# Revit family: 879-102X99-001-DN50-200
name_source: partatom
category: Pipe Accessories
units: mm (PartAtom-declared; Revit-internal decimal feet)

## family parameters
Always vertical = Yes
Cut with Voids When Loaded = No
Part Type = Valve - Breaks Into
Round Connector Dimension = Use Diameter
Shared = No
Work Plane-Based = No

## types (48) — shared parameters
879-0050-10-14400209999 = DN50_PN10/16
879-0050-10-144002099A0 = DN50_PN10/16
879-0050-10-14400219999 = DN50_PN10/16
879-0050-10-144002199A0 = DN50_PN10/16
879-0050-10-14400229999 = DN50_PN10/16
879-0050-10-144002299A0 = DN50_PN10/16
879-0065-10-14400209999 = DN65_PN10/16
879-0065-10-144002099A0 = DN65_PN10/16
879-0065-10-14400219999 = DN65_PN10/16
879-0065-10-144002199A0 = DN65_PN10/16
879-0065-10-14400229999 = DN65_PN10/16
879-0065-10-144002299A0 = DN65_PN10/16
879-0080-10-14400209999 = DN80_PN10/16
879-0080-10-144002099A0 = DN80_PN10/16
879-0080-10-14400219999 = DN80_PN10/16
879-0080-10-144002199A0 = DN80_PN10/16
879-0080-10-14400229999 = DN80_PN10/16
879-0080-10-144002299A0 = DN80_PN10/16
879-0100-10-14400209999 = DN100_PN10/16
879-0100-10-144002099A0 = DN100_PN10/16
879-0100-10-14400219999 = DN100_PN10/16
879-0100-10-144002199A0 = DN100_PN10/16
879-0100-10-14400229999 = DN100_PN10/16
879-0100-10-144002299A0 = DN100_PN10/16
879-0150-10-14400209999 = DN150_PN10/16
879-0150-10-144002099A0 = DN150_PN10/16
879-0150-10-14400219999 = DN150_PN10/16
879-0150-10-144002199A0 = DN150_PN10/16
879-0150-10-14400229999 = DN150_PN10/16
879-0150-10-144002299A0 = DN150_PN10/16
879-0150-10-14400239999 = DN150_PN10/16
879-0150-10-144002399A0 = DN150_PN10/16
879-0200-10-04400209999 = DN200_PN10
879-0200-10-044002099A0 = DN200_PN10
879-0200-10-04400219999 = DN200_PN10
879-0200-10-044002199A0 = DN200_PN10
879-0200-10-04400229999 = DN200_PN10
879-0200-10-044002299A0 = DN200_PN10
879-0200-10-04400239999 = DN200_PN10
879-0200-10-044002399A0 = DN200_PN10
879-0200-10-14400209999 = DN200_PN16
879-0200-10-144002099A0 = DN200_PN16
879-0200-10-14400219999 = DN200_PN16
879-0200-10-144002199A0 = DN200_PN16
879-0200-10-14400229999 = DN200_PN16
879-0200-10-144002299A0 = DN200_PN16
879-0200-10-14400239999 = DN200_PN16
879-0200-10-144002399A0 = DN200_PN16
Body_wall_thickness = 10 mm  [stored 0.0328084 ft]
Description_ = AVK CONSTANT FLOW CONTROL VALVE
Search_Table = 879-102X99-001-DN50-200
URL product pages = https://www.avkvalves.com

## per-type parameters (varying)
- 879-0050-10-14400209999_DN50_PN10/16: Body_Collar_Dia=23.96 mm; Body_Collar_Dia_2=20.63 mm; Body_Flange_Dia=74.19 mm; Body_Flange_Dia_2=82.14 mm; Body_Height_1=57.5 mm; Body_Height_2=28.75 mm; Body_Height_3=45 mm; Body_Height_4=43.75 mm; Body_Top_Dia=10.31 mm; Body_Top_Dia_2=8.59 mm; Body_With_Dia=57.5 mm; Body_With_Dia_2=62.16 mm; Bolt_support=153.33 mm; Bolt_support_2=76.67 mm; Bolt_support_Dia=12 mm  [stored 0.0393701 ft]; Bolt_support_lenght=45 mm; Bolt_support_lenght_2=55 mm; Bottom_profile=12.5 mm  [stored 0.0410105 ft]; D1=49.5 mm; DN=50 mm; FOD=82.5 mm; Fillet_Length=6 mm  [stored 0.019685 ft]; Flange_thickness=19 mm; H3=400 mm; ID=25 mm; L=230 mm; L1=247 mm; L_Ref=238.5 mm; PG_Dia=25 mm; PG_Ref=38.33 mm; PG_depth=8.4 mm  [stored 0.0275591 ft]; PG_ref=35 mm; Pilot_Dia_1=15 mm  [stored 0.0492126 ft]; Pilot_Dia_2=30 mm; Pilot_Dia_3=10 mm  [stored 0.0328084 ft]; Pilot_Dia_4=5 mm  [stored 0.0164042 ft]; Pilot_Dia_5=3.33 mm; Pilot_top_1=241.88 mm; Pilot_top_ref=75.63 mm; Profile1_Height=135 mm; Profile1_Length=22.3 mm; Profile1_Length_2=14.86 mm; Profile_Dia=6 mm  [stored 0.019685 ft]; Profile_Dia_2=6 mm  [stored 0.019685 ft]; Profile_Dia_3=12 mm  [stored 0.0393701 ft]; Top_Profile=92 mm; Top_Profile_Ref=97 mm; Top_Ref=166.25 mm; Top_Ref_2=204.06 mm; W=245 mm; W_Ref=242 mm
- 879-0050-10-144002099A0_DN50_PN10/16: Body_Collar_Dia=23.96 mm; Body_Collar_Dia_2=20.63 mm; Body_Flange_Dia=74.19 mm; Body_Flange_Dia_2=82.14 mm; Body_Height_1=57.5 mm; Body_Height_2=28.75 mm; Body_Height_3=50 mm; Body_Height_4=43.75 mm; Body_Top_Dia=10.31 mm; Body_Top_Dia_2=8.59 mm; Body_With_Dia=57.5 mm; Body_With_Dia_2=62.16 mm; Bolt_support=153.33 mm; Bolt_support_2=76.67 mm; Bolt_support_Dia=12 mm  [stored 0.0393701 ft]; Bolt_support_lenght=45.05 mm; Bolt_support_lenght_2=55.05 mm; Bottom_profile=12.53 mm; D1=49.5 mm; DN=50.1 mm; FOD=82.5 mm; Fillet_Length=6 mm  [stored 0.019685 ft]; Flange_thickness=19 mm; H3=407 mm; ID=25.05 mm; L=230 mm; L1=247 mm; L_Ref=238.5 mm; PG_Dia=25.05 mm; PG_Ref=38.33 mm; PG_depth=8.4 mm  [stored 0.0275591 ft]; PG_ref=35.05 mm; Pilot_Dia_1=15 mm  [stored 0.0492126 ft]; Pilot_Dia_2=30 mm; Pilot_Dia_3=10 mm  [stored 0.0328084 ft]; Pilot_Dia_4=5 mm  [stored 0.0164042 ft]; Pilot_Dia_5=3.33 mm; Pilot_top_1=247.88 mm; Pilot_top_ref=76.63 mm; Profile1_Height=145 mm; Profile1_Length=22.3 mm; Profile1_Length_2=14.86 mm; Profile_Dia=6 mm  [stored 0.019685 ft]; Profile_Dia_2=6 mm  [stored 0.019685 ft]; Profile_Dia_3=12 mm  [stored 0.0393701 ft]; Top_Profile=92 mm; Top_Profile_Ref=97 mm; Top_Ref=171.25 mm; Top_Ref_2=209.56 mm; W=245 mm; W_Ref=242 mm
- 879-0050-10-14400219999_DN50_PN10/16: Body_Collar_Dia=23.96 mm; Body_Collar_Dia_2=20.63 mm; Body_Flange_Dia=74.19 mm; Body_Flange_Dia_2=82.14 mm; Body_Height_1=57.5 mm; Body_Height_2=28.75 mm; Body_Height_3=45 mm; Body_Height_4=43.75 mm; Body_Top_Dia=10.31 mm; Body_Top_Dia_2=8.59 mm; Body_With_Dia=57.5 mm; Body_With_Dia_2=62.16 mm; Bolt_support=153.33 mm; Bolt_support_2=76.67 mm; Bolt_support_Dia=12 mm  [stored 0.0393701 ft]; Bolt_support_lenght=45.1 mm; Bolt_support_lenght_2=55.1 mm; Bottom_profile=12.55 mm  [stored 0.0411745 ft]; D1=49.5 mm; DN=50.2 mm; FOD=82.5 mm; Fillet_Length=6 mm  [stored 0.019685 ft]; Flange_thickness=19 mm; H3=400 mm; ID=25.1 mm; L=230 mm; L1=247 mm; L_Ref=238.5 mm; PG_Dia=25.1 mm; PG_Ref=38.33 mm; PG_depth=8.4 mm  [stored 0.0275591 ft]; PG_ref=35.1 mm; Pilot_Dia_1=15 mm  [stored 0.0492126 ft]; Pilot_Dia_2=30 mm; Pilot_Dia_3=10 mm  [stored 0.0328084 ft]; Pilot_Dia_4=5 mm  [stored 0.0164042 ft]; Pilot_Dia_5=3.33 mm; Pilot_top_1=241.88 mm; Pilot_top_ref=75.63 mm; Profile1_Height=135 mm; Profile1_Length=22.3 mm; Profile1_Length_2=14.86 mm; Profile_Dia=6 mm  [stored 0.019685 ft]; Profile_Dia_2=6 mm  [stored 0.019685 ft]; Profile_Dia_3=12 mm  [stored 0.0393701 ft]; Top_Profile=92 mm; Top_Profile_Ref=97 mm; Top_Ref=166.25 mm; Top_Ref_2=204.06 mm; W=245 mm; W_Ref=242 mm
- 879-0050-10-144002199A0_DN50_PN10/16: Body_Collar_Dia=23.96 mm; Body_Collar_Dia_2=20.63 mm; Body_Flange_Dia=74.19 mm; Body_Flange_Dia_2=82.14 mm; Body_Height_1=57.5 mm; Body_Height_2=28.75 mm; Body_Height_3=50 mm; Body_Height_4=43.75 mm; Body_Top_Dia=10.31 mm; Body_Top_Dia_2=8.59 mm; Body_With_Dia=57.5 mm; Body_With_Dia_2=62.16 mm; Bolt_support=153.33 mm; Bolt_support_2=76.67 mm; Bolt_support_Dia=12 mm  [stored 0.0393701 ft]; Bolt_support_lenght=45.15 mm; Bolt_support_lenght_2=55.15 mm; Bottom_profile=12.58 mm; D1=49.5 mm; DN=50.3 mm; FOD=82.5 mm; Fillet_Length=6 mm  [stored 0.019685 ft]; Flange_thickness=19 mm; H3=407 mm; ID=25.15 mm; L=230 mm; L1=247 mm; L_Ref=238.5 mm; PG_Dia=25.15 mm; PG_Ref=38.33 mm; PG_depth=8.4 mm  [stored 0.0275591 ft]; PG_ref=35.15 mm; Pilot_Dia_1=15 mm  [stored 0.0492126 ft]; Pilot_Dia_2=30 mm; Pilot_Dia_3=10 mm  [stored 0.0328084 ft]; Pilot_Dia_4=5 mm  [stored 0.0164042 ft]; Pilot_Dia_5=3.33 mm; Pilot_top_1=247.88 mm; Pilot_top_ref=76.63 mm; Profile1_Height=145 mm; Profile1_Length=22.3 mm; Profile1_Length_2=14.86 mm; Profile_Dia=6 mm  [stored 0.019685 ft]; Profile_Dia_2=6 mm  [stored 0.019685 ft]; Profile_Dia_3=12 mm  [stored 0.0393701 ft]; Top_Profile=92 mm; Top_Profile_Ref=97 mm; Top_Ref=171.25 mm; Top_Ref_2=209.56 mm; W=245 mm; W_Ref=242 mm
- 879-0050-10-14400229999_DN50_PN10/16: Body_Collar_Dia=23.96 mm; Body_Collar_Dia_2=20.63 mm; Body_Flange_Dia=74.19 mm; Body_Flange_Dia_2=82.14 mm; Body_Height_1=57.5 mm; Body_Height_2=28.75 mm; Body_Height_3=45 mm; Body_Height_4=43.75 mm; Body_Top_Dia=10.31 mm; Body_Top_Dia_2=8.59 mm; Body_With_Dia=57.5 mm; Body_With_Dia_2=62.16 mm; Bolt_support=153.33 mm; Bolt_support_2=76.67 mm; Bolt_support_Dia=12 mm  [stored 0.0393701 ft]; Bolt_support_lenght=45.2 mm; Bolt_support_lenght_2=55.2 mm; Bottom_profile=12.6 mm  [stored 0.0413386 ft]; D1=49.5 mm; DN=50.4 mm; FOD=82.5 mm; Fillet_Length=6 mm  [stored 0.019685 ft]; Flange_thickness=19 mm; H3=400 mm; ID=25.2 mm; L=230 mm; L1=247 mm; L_Ref=238.5 mm; PG_Dia=25.2 mm; PG_Ref=38.33 mm; PG_depth=8.4 mm  [stored 0.0275591 ft]; PG_ref=35.2 mm; Pilot_Dia_1=15 mm  [stored 0.0492126 ft]; Pilot_Dia_2=30 mm; Pilot_Dia_3=10 mm  [stored 0.0328084 ft]; Pilot_Dia_4=5 mm  [stored 0.0164042 ft]; Pilot_Dia_5=3.33 mm; Pilot_top_1=241.88 mm; Pilot_top_ref=75.63 mm; Profile1_Height=135 mm; Profile1_Length=22.3 mm; Profile1_Length_2=14.86 mm; Profile_Dia=6 mm  [stored 0.019685 ft]; Profile_Dia_2=6 mm  [stored 0.019685 ft]; Profile_Dia_3=12 mm  [stored 0.0393701 ft]; Top_Profile=92 mm; Top_Profile_Ref=97 mm; Top_Ref=166.25 mm; Top_Ref_2=204.06 mm; W=245 mm; W_Ref=242 mm
- 879-0050-10-144002299A0_DN50_PN10/16: Body_Collar_Dia=23.96 mm; Body_Collar_Dia_2=20.63 mm; Body_Flange_Dia=74.19 mm; Body_Flange_Dia_2=82.14 mm; Body_Height_1=57.5 mm; Body_Height_2=28.75 mm; Body_Height_3=50 mm; Body_Height_4=43.75 mm; Body_Top_Dia=10.31 mm; Body_Top_Dia_2=8.59 mm; Body_With_Dia=57.5 mm; Body_With_Dia_2=62.16 mm; Bolt_support=153.33 mm; Bolt_support_2=76.67 mm; Bolt_support_Dia=12 mm  [stored 0.0393701 ft]; Bolt_support_lenght=45.25 mm; Bolt_support_lenght_2=55.25 mm; Bottom_profile=12.63 mm; D1=49.5 mm; DN=50.5 mm; FOD=82.5 mm; Fillet_Length=6 mm  [stored 0.019685 ft]; Flange_thickness=19 mm; H3=407 mm; ID=25.25 mm; L=230 mm; L1=247 mm; L_Ref=238.5 mm; PG_Dia=25.25 mm; PG_Ref=38.33 mm; PG_depth=8.4 mm  [stored 0.0275591 ft]; PG_ref=35.25 mm; Pilot_Dia_1=15 mm  [stored 0.0492126 ft]; Pilot_Dia_2=30 mm; Pilot_Dia_3=10 mm  [stored 0.0328084 ft]; Pilot_Dia_4=5 mm  [stored 0.0164042 ft]; Pilot_Dia_5=3.33 mm; Pilot_top_1=247.88 mm; Pilot_top_ref=76.63 mm; Profile1_Height=145 mm; Profile1_Length=22.3 mm; Profile1_Length_2=14.86 mm; Profile_Dia=6 mm  [stored 0.019685 ft]; Profile_Dia_2=6 mm  [stored 0.019685 ft]; Profile_Dia_3=12 mm  [stored 0.0393701 ft]; Top_Profile=92 mm; Top_Profile_Ref=97 mm; Top_Ref=171.25 mm; Top_Ref_2=209.56 mm; W=245 mm; W_Ref=242 mm
- 879-0065-10-14400209999_DN65_PN10/16: Body_Collar_Dia=30.21 mm; Body_Collar_Dia_2=26.01 mm; Body_Flange_Dia=93.55 mm; Body_Flange_Dia_2=103.57 mm; Body_Height_1=72.5 mm; Body_Height_2=36.25 mm; Body_Height_3=58 mm; Body_Height_4=51.25 mm; Body_Top_Dia=13 mm; Body_Top_Dia_2=10.84 mm; Body_With_Dia=72.5 mm; Body_With_Dia_2=78.38 mm; Bolt_support=193.33 mm; Bolt_support_2=96.67 mm; Bolt_support_Dia=12 mm  [stored 0.0393701 ft]; Bolt_support_lenght=52.5 mm; Bolt_support_lenght_2=62.5 mm; Bottom_profile=16.25 mm  [stored 0.0533136 ft]; D1=59 mm; DN=65 mm; FOD=92.5 mm; Fillet_Length=6 mm  [stored 0.019685 ft]; Flange_thickness=19 mm; H3=425 mm; ID=32.5 mm; L=290 mm; L1=307 mm; L_Ref=298.5 mm; PG_Dia=32.5 mm; PG_Ref=48.33 mm; PG_depth=8.4 mm  [stored 0.0275591 ft]; PG_ref=42.5 mm; Pilot_Dia_1=17.5 mm; Pilot_Dia_2=35 mm; Pilot_Dia_3=11.67 mm; Pilot_Dia_4=5.83 mm; Pilot_Dia_5=3.89 mm; Pilot_top_1=267.13 mm; Pilot_top_ref=65.38 mm; Profile1_Height=152 mm; Profile1_Length=25 mm; Profile1_Length_2=16.67 mm; Profile_Dia=6 mm  [stored 0.019685 ft]; Profile_Dia_2=6 mm  [stored 0.019685 ft]; Profile_Dia_3=12 mm  [stored 0.0393701 ft]; Top_Profile=116 mm; Top_Profile_Ref=121 mm; Top_Ref=201.75 mm; Top_Ref_2=234.44 mm; W=255 mm; W_Ref=252 mm
- 879-0065-10-144002099A0_DN65_PN10/16: Body_Collar_Dia=30.21 mm; Body_Collar_Dia_2=26.01 mm; Body_Flange_Dia=93.55 mm; Body_Flange_Dia_2=103.57 mm; Body_Height_1=72.5 mm; Body_Height_2=36.25 mm; Body_Height_3=72.5 mm; Body_Height_4=51.25 mm; Body_Top_Dia=13 mm; Body_Top_Dia_2=10.84 mm; Body_With_Dia=72.5 mm; Body_With_Dia_2=78.38 mm; Bolt_support=193.33 mm; Bolt_support_2=96.67 mm; Bolt_support_Dia=12 mm  [stored 0.0393701 ft]; Bolt_support_lenght=52.55 mm; Bolt_support_lenght_2=62.55 mm; Bottom_profile=16.28 mm; D1=59 mm; DN=65.1 mm; FOD=92.5 mm; Fillet_Length=6 mm  [stored 0.019685 ft]; Flange_thickness=19 mm; H3=436 mm; ID=32.55 mm; L=290 mm; L1=307 mm; L_Ref=298.5 mm; PG_Dia=32.55 mm; PG_Ref=48.33 mm; PG_depth=8.4 mm  [stored 0.0275591 ft]; PG_ref=42.55 mm; Pilot_Dia_1=17.5 mm; Pilot_Dia_2=35 mm; Pilot_Dia_3=11.67 mm; Pilot_Dia_4=5.83 mm; Pilot_Dia_5=3.89 mm; Pilot_top_1=279.88 mm; Pilot_top_ref=63.63 mm; Profile1_Height=170 mm; Profile1_Length=25 mm; Profile1_Length_2=16.67 mm; Profile_Dia=6 mm  [stored 0.019685 ft]; Profile_Dia_2=6 mm  [stored 0.019685 ft]; Profile_Dia_3=12 mm  [stored 0.0393701 ft]; Top_Profile=116 mm; Top_Profile_Ref=121 mm; Top_Ref=216.25 mm; Top_Ref_2=248.06 mm; W=255 mm; W_Ref=252 mm
- 879-0065-10-14400219999_DN65_PN10/16: Body_Collar_Dia=30.21 mm; Body_Collar_Dia_2=26.01 mm; Body_Flange_Dia=93.55 mm; Body_Flange_Dia_2=103.57 mm; Body_Height_1=72.5 mm; Body_Height_2=36.25 mm; Body_Height_3=58 mm; Body_Height_4=51.25 mm; Body_Top_Dia=13 mm; Body_Top_Dia_2=10.84 mm; Body_With_Dia=72.5 mm; Body_With_Dia_2=78.38 mm; Bolt_support=193.33 mm; Bolt_support_2=96.67 mm; Bolt_support_Dia=12 mm  [stored 0.0393701 ft]; Bolt_support_lenght=52.6 mm; Bolt_support_lenght_2=62.6 mm; Bottom_profile=16.3 mm; D1=59 mm; DN=65.2 mm; FOD=92.5 mm; Fillet_Length=6 mm  [stored 0.019685 ft]; Flange_thickness=19 mm; H3=425 mm; ID=32.6 mm; L=290 mm; L1=307 mm; L_Ref=298.5 mm; PG_Dia=32.6 mm; PG_Ref=48.33 mm; PG_depth=8.4 mm  [stored 0.0275591 ft]; PG_ref=42.6 mm; Pilot_Dia_1=17.5 mm; Pilot_Dia_2=35 mm; Pilot_Dia_3=11.67 mm; Pilot_Dia_4=5.83 mm; Pilot_Dia_5=3.89 mm; Pilot_top_1=267.13 mm; Pilot_top_ref=65.38 mm; Profile1_Height=152 mm; Profile1_Length=25 mm; Profile1_Length_2=16.67 mm; Profile_Dia=6 mm  [stored 0.019685 ft]; Profile_Dia_2=6 mm  [stored 0.019685 ft]; Profile_Dia_3=12 mm  [stored 0.0393701 ft]; Top_Profile=116 mm; Top_Profile_Ref=121 mm; Top_Ref=201.75 mm; Top_Ref_2=234.44 mm; W=255 mm; W_Ref=252 mm
- 879-0065-10-144002199A0_DN65_PN10/16: Body_Collar_Dia=30.21 mm; Body_Collar_Dia_2=26.01 mm; Body_Flange_Dia=93.55 mm; Body_Flange_Dia_2=103.57 mm; Body_Height_1=72.5 mm; Body_Height_2=36.25 mm; Body_Height_3=72.5 mm; Body_Height_4=51.25 mm; Body_Top_Dia=13 mm; Body_Top_Dia_2=10.84 mm; Body_With_Dia=72.5 mm; Body_With_Dia_2=78.38 mm; Bolt_support=193.33 mm; Bolt_support_2=96.67 mm; Bolt_support_Dia=12 mm  [stored 0.0393701 ft]; Bolt_support_lenght=52.65 mm; Bolt_support_lenght_2=62.65 mm; Bottom_profile=16.33 mm; D1=59 mm; DN=65.3 mm; FOD=92.5 mm; Fillet_Length=6 mm  [stored 0.019685 ft]; Flange_thickness=19 mm; H3=436 mm; ID=32.65 mm; L=290 mm; L1=307 mm; L_Ref=298.5 mm; PG_Dia=32.65 mm; PG_Ref=48.33 mm; PG_depth=8.4 mm  [stored 0.0275591 ft]; PG_ref=42.65 mm; Pilot_Dia_1=17.5 mm; Pilot_Dia_2=35 mm; Pilot_Dia_3=11.67 mm; Pilot_Dia_4=5.83 mm; Pilot_Dia_5=3.89 mm; Pilot_top_1=279.88 mm; Pilot_top_ref=63.63 mm; Profile1_Height=170 mm; Profile1_Length=25 mm; Profile1_Length_2=16.67 mm; Profile_Dia=6 mm  [stored 0.019685 ft]; Profile_Dia_2=6 mm  [stored 0.019685 ft]; Profile_Dia_3=12 mm  [stored 0.0393701 ft]; Top_Profile=116 mm; Top_Profile_Ref=121 mm; Top_Ref=216.25 mm; Top_Ref_2=248.06 mm; W=255 mm; W_Ref=252 mm
- 879-0065-10-14400229999_DN65_PN10/16: Body_Collar_Dia=30.21 mm; Body_Collar_Dia_2=26.01 mm; Body_Flange_Dia=93.55 mm; Body_Flange_Dia_2=103.57 mm; Body_Height_1=72.5 mm; Body_Height_2=36.25 mm; Body_Height_3=58 mm; Body_Height_4=51.25 mm; Body_Top_Dia=13 mm; Body_Top_Dia_2=10.84 mm; Body_With_Dia=72.5 mm; Body_With_Dia_2=78.38 mm; Bolt_support=193.33 mm; Bolt_support_2=96.67 mm; Bolt_support_Dia=12 mm  [stored 0.0393701 ft]; Bolt_support_lenght=52.7 mm; Bolt_support_lenght_2=62.7 mm; Bottom_profile=16.35 mm; D1=59 mm; DN=65.4 mm; FOD=92.5 mm; Fillet_Length=6 mm  [stored 0.019685 ft]; Flange_thickness=19 mm; H3=425 mm; ID=32.7 mm; L=290 mm; L1=307 mm; L_Ref=298.5 mm; PG_Dia=32.7 mm; PG_Ref=48.33 mm; PG_depth=8.4 mm  [stored 0.0275591 ft]; PG_ref=42.7 mm; Pilot_Dia_1=17.5 mm; Pilot_Dia_2=35 mm; Pilot_Dia_3=11.67 mm; Pilot_Dia_4=5.83 mm; Pilot_Dia_5=3.89 mm; Pilot_top_1=267.13 mm; Pilot_top_ref=65.38 mm; Profile1_Height=152 mm; Profile1_Length=25 mm; Profile1_Length_2=16.67 mm; Profile_Dia=6 mm  [stored 0.019685 ft]; Profile_Dia_2=6 mm  [stored 0.019685 ft]; Profile_Dia_3=12 mm  [stored 0.0393701 ft]; Top_Profile=116 mm; Top_Profile_Ref=121 mm; Top_Ref=201.75 mm; Top_Ref_2=234.44 mm; W=255 mm; W_Ref=252 mm
- 879-0065-10-144002299A0_DN65_PN10/16: Body_Collar_Dia=30.21 mm; Body_Collar_Dia_2=26.01 mm; Body_Flange_Dia=93.55 mm; Body_Flange_Dia_2=103.57 mm; Body_Height_1=72.5 mm; Body_Height_2=36.25 mm; Body_Height_3=72.5 mm; Body_Height_4=51.25 mm; Body_Top_Dia=13 mm; Body_Top_Dia_2=10.84 mm; Body_With_Dia=72.5 mm; Body_With_Dia_2=78.38 mm; Bolt_support=193.33 mm; Bolt_support_2=96.67 mm; Bolt_support_Dia=12 mm  [stored 0.0393701 ft]; Bolt_support_lenght=52.75 mm; Bolt_support_lenght_2=62.75 mm; Bottom_profile=16.38 mm; D1=59 mm; DN=65.5 mm; FOD=92.5 mm; Fillet_Length=6 mm  [stored 0.019685 ft]; Flange_thickness=19 mm; H3=436 mm; ID=32.75 mm; L=290 mm; L1=307 mm; L_Ref=298.5 mm; PG_Dia=32.75 mm; PG_Ref=48.33 mm; PG_depth=8.4 mm  [stored 0.0275591 ft]; PG_ref=42.75 mm; Pilot_Dia_1=17.5 mm; Pilot_Dia_2=35 mm; Pilot_Dia_3=11.67 mm; Pilot_Dia_4=5.83 mm; Pilot_Dia_5=3.89 mm; Pilot_top_1=279.88 mm; Pilot_top_ref=63.63 mm; Profile1_Height=170 mm; Profile1_Length=25 mm; Profile1_Length_2=16.67 mm; Profile_Dia=6 mm  [stored 0.019685 ft]; Profile_Dia_2=6 mm  [stored 0.019685 ft]; Profile_Dia_3=12 mm  [stored 0.0393701 ft]; Top_Profile=116 mm; Top_Profile_Ref=121 mm; Top_Ref=216.25 mm; Top_Ref_2=248.06 mm; W=255 mm; W_Ref=252 mm
- 879-0080-10-14400209999_DN80_PN10/16: Body_Collar_Dia=32.29 mm; Body_Collar_Dia_2=27.8 mm; Body_Flange_Dia=100 mm; Body_Flange_Dia_2=110.71 mm; Body_Height_1=77.5 mm; Body_Height_2=38.75 mm; Body_Height_3=62 mm; Body_Height_4=53.75 mm; Body_Top_Dia=13.9 mm; Body_Top_Dia_2=11.58 mm; Body_With_Dia=77.5 mm; Body_With_Dia_2=83.78 mm; Bolt_support=206.67 mm; Bolt_support_2=103.33 mm; Bolt_support_Dia=12 mm  [stored 0.0393701 ft]; Bolt_support_lenght=60 mm; Bolt_support_lenght_2=70 mm; Bottom_profile=20 mm; D1=66 mm; DN=80 mm; FOD=100 mm; Fillet_Length=6 mm  [stored 0.019685 ft]; Flange_thickness=19 mm; H3=440 mm; ID=40 mm; L=310 mm; L1=327 mm; L_Ref=318.5 mm; PG_Dia=40 mm; PG_Ref=51.67 mm; PG_depth=8.4 mm  [stored 0.0275591 ft]; PG_ref=50 mm; Pilot_Dia_1=19.5 mm; Pilot_Dia_2=39 mm; Pilot_Dia_3=13 mm; Pilot_Dia_4=6.5 mm; Pilot_Dia_5=4.33 mm; Pilot_top_1=276.63 mm; Pilot_top_ref=63.38 mm; Profile1_Height=179 mm; Profile1_Length=27.03 mm; Profile1_Length_2=18.02 mm; Profile_Dia=6 mm  [stored 0.019685 ft]; Profile_Dia_2=6 mm  [stored 0.019685 ft]; Profile_Dia_3=12 mm  [stored 0.0393701 ft]; Top_Profile=124 mm; Top_Profile_Ref=129 mm; Top_Ref=213.25 mm; Top_Ref_2=244.94 mm; W=270 mm; W_Ref=267 mm
- 879-0080-10-144002099A0_DN80_PN10/16: Body_Collar_Dia=32.29 mm; Body_Collar_Dia_2=27.8 mm; Body_Flange_Dia=100 mm; Body_Flange_Dia_2=110.71 mm; Body_Height_1=77.5 mm; Body_Height_2=38.75 mm; Body_Height_3=77.5 mm; Body_Height_4=53.75 mm; Body_Top_Dia=13.9 mm; Body_Top_Dia_2=11.58 mm; Body_With_Dia=77.5 mm; Body_With_Dia_2=83.78 mm; Bolt_support=206.67 mm; Bolt_support_2=103.33 mm; Bolt_support_Dia=12 mm  [stored 0.0393701 ft]; Bolt_support_lenght=60.05 mm; Bolt_support_lenght_2=70.05 mm; Bottom_profile=20.03 mm; D1=66 mm; DN=80.1 mm; FOD=100 mm; Fillet_Length=6 mm  [stored 0.019685 ft]; Flange_thickness=19 mm; H3=451 mm; ID=40.05 mm; L=310 mm; L1=327 mm; L_Ref=318.5 mm; PG_Dia=40.05 mm; PG_Ref=51.67 mm; PG_depth=8.4 mm  [stored 0.0275591 ft]; PG_ref=50.05 mm; Pilot_Dia_1=19.5 mm; Pilot_Dia_2=39 mm; Pilot_Dia_3=13 mm; Pilot_Dia_4=6.5 mm; Pilot_Dia_5=4.33 mm; Pilot_top_1=289.88 mm; Pilot_top_ref=61.13 mm; Profile1_Height=168 mm; Profile1_Length=27.03 mm; Profile1_Length_2=18.02 mm; Profile_Dia=6 mm  [stored 0.019685 ft]; Profile_Dia_2=6 mm  [stored 0.019685 ft]; Profile_Dia_3=12 mm  [stored 0.0393701 ft]; Top_Profile=124 mm; Top_Profile_Ref=129 mm; Top_Ref=228.75 mm; Top_Ref_2=259.31 mm; W=270 mm; W_Ref=267 mm
- 879-0080-10-14400219999_DN80_PN10/16: Body_Collar_Dia=32.29 mm; Body_Collar_Dia_2=27.8 mm; Body_Flange_Dia=100 mm; Body_Flange_Dia_2=110.71 mm; Body_Height_1=77.5 mm; Body_Height_2=38.75 mm; Body_Height_3=62 mm; Body_Height_4=53.75 mm; Body_Top_Dia=13.9 mm; Body_Top_Dia_2=11.58 mm; Body_With_Dia=77.5 mm; Body_With_Dia_2=83.78 mm; Bolt_support=206.67 mm; Bolt_support_2=103.33 mm; Bolt_support_Dia=12 mm  [stored 0.0393701 ft]; Bolt_support_lenght=60.1 mm; Bolt_support_lenght_2=70.1 mm; Bottom_profile=20.05 mm; D1=66 mm; DN=80.2 mm; FOD=100 mm; Fillet_Length=6 mm  [stored 0.019685 ft]; Flange_thickness=19 mm; H3=440 mm; ID=40.1 mm; L=310 mm; L1=327 mm; L_Ref=318.5 mm; PG_Dia=40.1 mm; PG_Ref=51.67 mm; PG_depth=8.4 mm  [stored 0.0275591 ft]; PG_ref=50.1 mm; Pilot_Dia_1=19.5 mm; Pilot_Dia_2=39 mm; Pilot_Dia_3=13 mm; Pilot_Dia_4=6.5 mm; Pilot_Dia_5=4.33 mm; Pilot_top_1=276.63 mm; Pilot_top_ref=63.38 mm; Profile1_Height=179 mm; Profile1_Length=27.03 mm; Profile1_Length_2=18.02 mm; Profile_Dia=6 mm  [stored 0.019685 ft]; Profile_Dia_2=6 mm  [stored 0.019685 ft]; Profile_Dia_3=12 mm  [stored 0.0393701 ft]; Top_Profile=124 mm; Top_Profile_Ref=129 mm; Top_Ref=213.25 mm; Top_Ref_2=244.94 mm; W=270 mm; W_Ref=267 mm
- 879-0080-10-144002199A0_DN80_PN10/16: Body_Collar_Dia=32.29 mm; Body_Collar_Dia_2=27.8 mm; Body_Flange_Dia=100 mm; Body_Flange_Dia_2=110.71 mm; Body_Height_1=77.5 mm; Body_Height_2=38.75 mm; Body_Height_3=77.5 mm; Body_Height_4=53.75 mm; Body_Top_Dia=13.9 mm; Body_Top_Dia_2=11.58 mm; Body_With_Dia=77.5 mm; Body_With_Dia_2=83.78 mm; Bolt_support=206.67 mm; Bolt_support_2=103.33 mm; Bolt_support_Dia=12 mm  [stored 0.0393701 ft]; Bolt_support_lenght=60.15 mm; Bolt_support_lenght_2=70.15 mm; Bottom_profile=20.08 mm; D1=66 mm; DN=80.3 mm; FOD=100 mm; Fillet_Length=6 mm  [stored 0.019685 ft]; Flange_thickness=19 mm; H3=451 mm; ID=40.15 mm; L=310 mm; L1=327 mm; L_Ref=318.5 mm; PG_Dia=40.15 mm; PG_Ref=51.67 mm; PG_depth=8.4 mm  [stored 0.0275591 ft]; PG_ref=50.15 mm; Pilot_Dia_1=19.5 mm; Pilot_Dia_2=39 mm; Pilot_Dia_3=13 mm; Pilot_Dia_4=6.5 mm; Pilot_Dia_5=4.33 mm; Pilot_top_1=289.88 mm; Pilot_top_ref=61.13 mm; Profile1_Height=168 mm; Profile1_Length=27.03 mm; Profile1_Length_2=18.02 mm; Profile_Dia=6 mm  [stored 0.019685 ft]; Profile_Dia_2=6 mm  [stored 0.019685 ft]; Profile_Dia_3=12 mm  [stored 0.0393701 ft]; Top_Profile=124 mm; Top_Profile_Ref=129 mm; Top_Ref=228.75 mm; Top_Ref_2=259.31 mm; W=270 mm; W_Ref=267 mm
- 879-0080-10-14400229999_DN80_PN10/16: Body_Collar_Dia=32.29 mm; Body_Collar_Dia_2=27.8 mm; Body_Flange_Dia=100 mm; Body_Flange_Dia_2=110.71 mm; Body_Height_1=77.5 mm; Body_Height_2=38.75 mm; Body_Height_3=62 mm; Body_Height_4=53.75 mm; Body_Top_Dia=13.9 mm; Body_Top_Dia_2=11.58 mm; Body_With_Dia=77.5 mm; Body_With_Dia_2=83.78 mm; Bolt_support=206.67 mm; Bolt_support_2=103.33 mm; Bolt_support_Dia=12 mm  [stored 0.0393701 ft]; Bolt_support_lenght=60.2 mm; Bolt_support_lenght_2=70.2 mm; Bottom_profile=20.1 mm; D1=66 mm; DN=80.4 mm; FOD=100 mm; Fillet_Length=6 mm  [stored 0.019685 ft]; Flange_thickness=19 mm; H3=440 mm; ID=40.2 mm; L=310 mm; L1=327 mm; L_Ref=318.5 mm; PG_Dia=40.2 mm; PG_Ref=51.67 mm; PG_depth=8.4 mm  [stored 0.0275591 ft]; PG_ref=50.2 mm; Pilot_Dia_1=19.5 mm; Pilot_Dia_2=39 mm; Pilot_Dia_3=13 mm; Pilot_Dia_4=6.5 mm; Pilot_Dia_5=4.33 mm; Pilot_top_1=276.63 mm; Pilot_top_ref=63.38 mm; Profile1_Height=179 mm; Profile1_Length=27.03 mm; Profile1_Length_2=18.02 mm; Profile_Dia=6 mm  [stored 0.019685 ft]; Profile_Dia_2=6 mm  [stored 0.019685 ft]; Profile_Dia_3=12 mm  [stored 0.0393701 ft]; Top_Profile=124 mm; Top_Profile_Ref=129 mm; Top_Ref=213.25 mm; Top_Ref_2=244.94 mm; W=270 mm; W_Ref=267 mm
- 879-0080-10-144002299A0_DN80_PN10/16: Body_Collar_Dia=32.29 mm; Body_Collar_Dia_2=27.8 mm; Body_Flange_Dia=100 mm; Body_Flange_Dia_2=110.71 mm; Body_Height_1=77.5 mm; Body_Height_2=38.75 mm; Body_Height_3=77.5 mm; Body_Height_4=53.75 mm; Body_Top_Dia=13.9 mm; Body_Top_Dia_2=11.58 mm; Body_With_Dia=77.5 mm; Body_With_Dia_2=83.78 mm; Bolt_support=206.67 mm; Bolt_support_2=103.33 mm; Bolt_support_Dia=12 mm  [stored 0.0393701 ft]; Bolt_support_lenght=60.25 mm; Bolt_support_lenght_2=70.25 mm; Bottom_profile=20.13 mm; D1=66 mm; DN=80.5 mm; FOD=100 mm; Fillet_Length=6 mm  [stored 0.019685 ft]; Flange_thickness=19 mm; H3=451 mm; ID=40.25 mm; L=310 mm; L1=327 mm; L_Ref=318.5 mm; PG_Dia=40.25 mm; PG_Ref=51.67 mm; PG_depth=8.4 mm  [stored 0.0275591 ft]; PG_ref=50.25 mm; Pilot_Dia_1=19.5 mm; Pilot_Dia_2=39 mm; Pilot_Dia_3=13 mm; Pilot_Dia_4=6.5 mm; Pilot_Dia_5=4.33 mm; Pilot_top_1=289.88 mm; Pilot_top_ref=61.13 mm; Profile1_Height=168 mm; Profile1_Length=27.03 mm; Profile1_Length_2=18.02 mm; Profile_Dia=6 mm  [stored 0.019685 ft]; Profile_Dia_2=6 mm  [stored 0.019685 ft]; Profile_Dia_3=12 mm  [stored 0.0393701 ft]; Top_Profile=124 mm; Top_Profile_Ref=129 mm; Top_Ref=228.75 mm; Top_Ref_2=259.31 mm; W=270 mm; W_Ref=267 mm
- 879-0100-10-14400209999_DN100_PN10/16: Body_Collar_Dia=36.46 mm; Body_Collar_Dia_2=31.39 mm; Body_Flange_Dia=112.9 mm; Body_Flange_Dia_2=125 mm; Body_Height_1=87.5 mm; Body_Height_2=43.75 mm; Body_Height_3=58.5 mm; Body_Height_4=58.75 mm; Body_Top_Dia=15.7 mm; Body_Top_Dia_2=13.08 mm; Body_With_Dia=87.5 mm; Body_With_Dia_2=94.59 mm; Bolt_support=233.33 mm; Bolt_support_2=116.67 mm; Bolt_support_Dia=12 mm  [stored 0.0393701 ft]; Bolt_support_lenght=70 mm; Bolt_support_lenght_2=80 mm; Bottom_profile=25 mm; D1=78 mm; DN=100 mm; FOD=110 mm; Fillet_Length=6 mm  [stored 0.019685 ft]; Flange_thickness=19 mm; H3=460 mm; ID=50 mm; L=350 mm; L1=367 mm; L_Ref=358.5 mm; PG_Dia=50 mm; PG_Ref=58.33 mm; PG_depth=8.4 mm  [stored 0.0275591 ft]; PG_ref=60 mm; Pilot_Dia_1=22 mm; Pilot_Dia_2=44 mm; Pilot_Dia_3=14.67 mm; Pilot_Dia_4=7.33 mm; Pilot_Dia_5=4.89 mm; Pilot_top_1=287.38 mm; Pilot_top_ref=62.63 mm; Profile1_Height=185 mm; Profile1_Length=29.73 mm; Profile1_Length_2=19.82 mm; Profile_Dia=6 mm  [stored 0.019685 ft]; Profile_Dia_2=6 mm  [stored 0.019685 ft]; Profile_Dia_3=12 mm  [stored 0.0393701 ft]; Top_Profile=140 mm; Top_Profile_Ref=145 mm; Top_Ref=224.75 mm; Top_Ref_2=256.06 mm; W=290 mm; W_Ref=287 mm
- 879-0100-10-144002099A0_DN100_PN10/16: Body_Collar_Dia=36.46 mm; Body_Collar_Dia_2=31.39 mm; Body_Flange_Dia=112.9 mm; Body_Flange_Dia_2=125 mm; Body_Height_1=87.5 mm; Body_Height_2=43.75 mm; Body_Height_3=70 mm; Body_Height_4=58.75 mm; Body_Top_Dia=15.7 mm; Body_Top_Dia_2=13.08 mm; Body_With_Dia=87.5 mm; Body_With_Dia_2=94.59 mm; Bolt_support=233.33 mm; Bolt_support_2=116.67 mm; Bolt_support_Dia=12 mm  [stored 0.0393701 ft]; Bolt_support_lenght=70.05 mm; Bolt_support_lenght_2=80.05 mm; Bottom_profile=25.03 mm; D1=78 mm; DN=100.1 mm; FOD=110 mm; Fillet_Length=6 mm  [stored 0.019685 ft]; Flange_thickness=19 mm; H3=474 mm; ID=50.05 mm; L=350 mm; L1=367 mm; L_Ref=358.5 mm; PG_Dia=50.05 mm; PG_Ref=58.33 mm; PG_depth=8.4 mm  [stored 0.0275591 ft]; PG_ref=60.05 mm; Pilot_Dia_1=22 mm; Pilot_Dia_2=44 mm; Pilot_Dia_3=14.67 mm; Pilot_Dia_4=7.33 mm; Pilot_Dia_5=4.89 mm; Pilot_top_1=300.13 mm; Pilot_top_ref=63.88 mm; Profile1_Height=176 mm; Profile1_Length=29.73 mm; Profile1_Length_2=19.82 mm; Profile_Dia=6 mm  [stored 0.019685 ft]; Profile_Dia_2=6 mm  [stored 0.019685 ft]; Profile_Dia_3=12 mm  [stored 0.0393701 ft]; Top_Profile=140 mm; Top_Profile_Ref=145 mm; Top_Ref=236.25 mm; Top_Ref_2=268.19 mm; W=290 mm; W_Ref=287 mm
- 879-0100-10-14400219999_DN100_PN10/16: Body_Collar_Dia=36.46 mm; Body_Collar_Dia_2=31.39 mm; Body_Flange_Dia=112.9 mm; Body_Flange_Dia_2=125 mm; Body_Height_1=87.5 mm; Body_Height_2=43.75 mm; Body_Height_3=58.5 mm; Body_Height_4=58.75 mm; Body_Top_Dia=15.7 mm; Body_Top_Dia_2=13.08 mm; Body_With_Dia=87.5 mm; Body_With_Dia_2=94.59 mm; Bolt_support=233.33 mm; Bolt_support_2=116.67 mm; Bolt_support_Dia=12 mm  [stored 0.0393701 ft]; Bolt_support_lenght=70.1 mm; Bolt_support_lenght_2=80.1 mm; Bottom_profile=25.05 mm; D1=78 mm; DN=100.2 mm; FOD=110 mm; Fillet_Length=6 mm  [stored 0.019685 ft]; Flange_thickness=19 mm; H3=460 mm; ID=50.1 mm; L=350 mm; L1=367 mm; L_Ref=358.5 mm; PG_Dia=50.1 mm; PG_Ref=58.33 mm; PG_depth=8.4 mm  [stored 0.0275591 ft]; PG_ref=60.1 mm; Pilot_Dia_1=22 mm; Pilot_Dia_2=44 mm; Pilot_Dia_3=14.67 mm; Pilot_Dia_4=7.33 mm; Pilot_Dia_5=4.89 mm; Pilot_top_1=287.38 mm; Pilot_top_ref=62.63 mm; Profile1_Height=185 mm; Profile1_Length=29.73 mm; Profile1_Length_2=19.82 mm; Profile_Dia=6 mm  [stored 0.019685 ft]; Profile_Dia_2=6 mm  [stored 0.019685 ft]; Profile_Dia_3=12 mm  [stored 0.0393701 ft]; Top_Profile=140 mm; Top_Profile_Ref=145 mm; Top_Ref=224.75 mm; Top_Ref_2=256.06 mm; W=290 mm; W_Ref=287 mm
- 879-0100-10-144002199A0_DN100_PN10/16: Body_Collar_Dia=36.46 mm; Body_Collar_Dia_2=31.39 mm; Body_Flange_Dia=112.9 mm; Body_Flange_Dia_2=125 mm; Body_Height_1=87.5 mm; Body_Height_2=43.75 mm; Body_Height_3=70 mm; Body_Height_4=58.75 mm; Body_Top_Dia=15.7 mm; Body_Top_Dia_2=13.08 mm; Body_With_Dia=87.5 mm; Body_With_Dia_2=94.59 mm; Bolt_support=233.33 mm; Bolt_support_2=116.67 mm; Bolt_support_Dia=12 mm  [stored 0.0393701 ft]; Bolt_support_lenght=70.15 mm; Bolt_support_lenght_2=80.15 mm; Bottom_profile=25.08 mm; D1=78 mm; DN=100.3 mm; FOD=110 mm; Fillet_Length=6 mm  [stored 0.019685 ft]; Flange_thickness=19 mm; H3=474 mm; ID=50.15 mm; L=350 mm; L1=367 mm; L_Ref=358.5 mm; PG_Dia=50.15 mm; PG_Ref=58.33 mm; PG_depth=8.4 mm  [stored 0.0275591 ft]; PG_ref=60.15 mm; Pilot_Dia_1=22 mm; Pilot_Dia_2=44 mm; Pilot_Dia_3=14.67 mm; Pilot_Dia_4=7.33 mm; Pilot_Dia_5=4.89 mm; Pilot_top_1=300.13 mm; Pilot_top_ref=63.88 mm; Profile1_Height=176 mm; Profile1_Length=29.73 mm; Profile1_Length_2=19.82 mm; Profile_Dia=6 mm  [stored 0.019685 ft]; Profile_Dia_2=6 mm  [stored 0.019685 ft]; Profile_Dia_3=12 mm  [stored 0.0393701 ft]; Top_Profile=140 mm; Top_Profile_Ref=145 mm; Top_Ref=236.25 mm; Top_Ref_2=268.19 mm; W=290 mm; W_Ref=287 mm
- 879-0100-10-14400229999_DN100_PN10/16: Body_Collar_Dia=36.46 mm; Body_Collar_Dia_2=31.39 mm; Body_Flange_Dia=112.9 mm; Body_Flange_Dia_2=125 mm; Body_Height_1=87.5 mm; Body_Height_2=43.75 mm; Body_Height_3=58.5 mm; Body_Height_4=58.75 mm; Body_Top_Dia=15.7 mm; Body_Top_Dia_2=13.08 mm; Body_With_Dia=87.5 mm; Body_With_Dia_2=94.59 mm; Bolt_support=233.33 mm; Bolt_support_2=116.67 mm; Bolt_support_Dia=12 mm  [stored 0.0393701 ft]; Bolt_support_lenght=70.2 mm; Bolt_support_lenght_2=80.2 mm; Bottom_profile=25.1 mm; D1=78 mm; DN=100.4 mm; FOD=110 mm; Fillet_Length=6 mm  [stored 0.019685 ft]; Flange_thickness=19 mm; H3=460 mm; ID=50.2 mm; L=350 mm; L1=367 mm; L_Ref=358.5 mm; PG_Dia=50.2 mm; PG_Ref=58.33 mm; PG_depth=8.4 mm  [stored 0.0275591 ft]; PG_ref=60.2 mm; Pilot_Dia_1=22 mm; Pilot_Dia_2=44 mm; Pilot_Dia_3=14.67 mm; Pilot_Dia_4=7.33 mm; Pilot_Dia_5=4.89 mm; Pilot_top_1=287.38 mm; Pilot_top_ref=62.63 mm; Profile1_Height=185 mm; Profile1_Length=29.73 mm; Profile1_Length_2=19.82 mm; Profile_Dia=6 mm  [stored 0.019685 ft]; Profile_Dia_2=6 mm  [stored 0.019685 ft]; Profile_Dia_3=12 mm  [stored 0.0393701 ft]; Top_Profile=140 mm; Top_Profile_Ref=145 mm; Top_Ref=224.75 mm; Top_Ref_2=256.06 mm; W=290 mm; W_Ref=287 mm
- 879-0100-10-144002299A0_DN100_PN10/16: Body_Collar_Dia=36.46 mm; Body_Collar_Dia_2=31.39 mm; Body_Flange_Dia=112.9 mm; Body_Flange_Dia_2=125 mm; Body_Height_1=87.5 mm; Body_Height_2=43.75 mm; Body_Height_3=70 mm; Body_Height_4=58.75 mm; Body_Top_Dia=15.7 mm; Body_Top_Dia_2=13.08 mm; Body_With_Dia=87.5 mm; Body_With_Dia_2=94.59 mm; Bolt_support=233.33 mm; Bolt_support_2=116.67 mm; Bolt_support_Dia=12 mm  [stored 0.0393701 ft]; Bolt_support_lenght=70.25 mm; Bolt_support_lenght_2=80.25 mm; Bottom_profile=25.13 mm; D1=78 mm; DN=100.5 mm; FOD=110 mm; Fillet_Length=6 mm  [stored 0.019685 ft]; Flange_thickness=19 mm; H3=474 mm; ID=50.25 mm; L=350 mm; L1=367 mm; L_Ref=358.5 mm; PG_Dia=50.25 mm; PG_Ref=58.33 mm; PG_depth=8.4 mm  [stored 0.0275591 ft]; PG_ref=60.25 mm; Pilot_Dia_1=22 mm; Pilot_Dia_2=44 mm; Pilot_Dia_3=14.67 mm; Pilot_Dia_4=7.33 mm; Pilot_Dia_5=4.89 mm; Pilot_top_1=300.13 mm; Pilot_top_ref=63.88 mm; Profile1_Height=176 mm; Profile1_Length=29.73 mm; Profile1_Length_2=19.82 mm; Profile_Dia=6 mm  [stored 0.019685 ft]; Profile_Dia_2=6 mm  [stored 0.019685 ft]; Profile_Dia_3=12 mm  [stored 0.0393701 ft]; Top_Profile=140 mm; Top_Profile_Ref=145 mm; Top_Ref=236.25 mm; Top_Ref_2=268.19 mm; W=290 mm; W_Ref=287 mm
- 879-0150-10-14400209999_DN150_PN10/16: Body_Collar_Dia=50 mm; Body_Collar_Dia_2=43.05 mm; Body_Flange_Dia=154.84 mm; Body_Flange_Dia_2=171.43 mm; Body_Height_1=120 mm; Body_Height_2=60 mm; Body_Height_3=60 mm; Body_Height_4=75 mm; Body_Top_Dia=21.52 mm; Body_Top_Dia_2=17.94 mm; Body_With_Dia=120 mm; Body_With_Dia_2=129.73 mm; Bolt_support=320 mm; Bolt_support_2=160 mm; Bolt_support_Dia=16 mm  [stored 0.0524934 ft]; Bolt_support_lenght=95 mm; Bolt_support_lenght_2=105 mm; Bottom_profile=37.5 mm; D1=105.5 mm; DN=150 mm; FOD=142.5 mm; Fillet_Length=8 mm  [stored 0.0262467 ft]; Flange_thickness=19 mm; H3=590 mm; ID=75 mm; L=480 mm; L1=497 mm; L_Ref=488.5 mm; PG_Dia=50 mm; PG_Ref=80 mm; PG_depth=11.2 mm  [stored 0.0367454 ft]; PG_ref=85 mm; Pilot_Dia_1=31 mm; Pilot_Dia_2=62 mm; Pilot_Dia_3=20.67 mm; Pilot_Dia_4=10.33 mm; Pilot_Dia_5=6.89 mm; Pilot_top_1=361.25 mm; Pilot_top_ref=86.25 mm; Profile1_Height=230 mm; Profile1_Length=38.51 mm; Profile1_Length_2=25.68 mm; Profile_Dia=8 mm  [stored 0.0262467 ft]; Profile_Dia_2=8 mm  [stored 0.0262467 ft]; Profile_Dia_3=16 mm  [stored 0.0524934 ft]; Top_Profile=192 mm; Top_Profile_Ref=197 mm; Top_Ref=275 mm; Top_Ref_2=318.13 mm; W=410 mm; W_Ref=406 mm
- 879-0150-10-144002099A0_DN150_PN10/16: Body_Collar_Dia=50 mm; Body_Collar_Dia_2=43.05 mm; Body_Flange_Dia=154.84 mm; Body_Flange_Dia_2=171.43 mm; Body_Height_1=120 mm; Body_Height_2=60 mm; Body_Height_3=68 mm; Body_Height_4=75 mm; Body_Top_Dia=21.52 mm; Body_Top_Dia_2=17.94 mm; Body_With_Dia=120 mm; Body_With_Dia_2=129.73 mm; Bolt_support=320 mm; Bolt_support_2=160 mm; Bolt_support_Dia=16 mm  [stored 0.0524934 ft]; Bolt_support_lenght=95.05 mm; Bolt_support_lenght_2=105.05 mm; Bottom_profile=37.53 mm; D1=105.5 mm; DN=150.1 mm; FOD=142.5 mm; Fillet_Length=8 mm  [stored 0.0262467 ft]; Flange_thickness=19 mm; H3=607 mm; ID=75.05 mm; L=480 mm; L1=497 mm; L_Ref=488.5 mm; PG_Dia=50.03 mm; PG_Ref=80 mm; PG_depth=11.2 mm  [stored 0.0367454 ft]; PG_ref=85.05 mm; Pilot_Dia_1=31 mm; Pilot_Dia_2=62 mm; Pilot_Dia_3=20.67 mm; Pilot_Dia_4=10.33 mm; Pilot_Dia_5=6.89 mm; Pilot_top_1=373.75 mm; Pilot_top_ref=90.75 mm; Profile1_Height=230 mm; Profile1_Length=38.51 mm; Profile1_Length_2=25.68 mm; Profile_Dia=8 mm  [stored 0.0262467 ft]; Profile_Dia_2=8 mm  [stored 0.0262467 ft]; Profile_Dia_3=16 mm  [stored 0.0524934 ft]; Top_Profile=192 mm; Top_Profile_Ref=197 mm; Top_Ref=283 mm; Top_Ref_2=328.38 mm; W=410 mm; W_Ref=406 mm
- 879-0150-10-14400219999_DN150_PN10/16: Body_Collar_Dia=50 mm; Body_Collar_Dia_2=43.05 mm; Body_Flange_Dia=154.84 mm; Body_Flange_Dia_2=171.43 mm; Body_Height_1=120 mm; Body_Height_2=60 mm; Body_Height_3=60 mm; Body_Height_4=75 mm; Body_Top_Dia=21.52 mm; Body_Top_Dia_2=17.94 mm; Body_With_Dia=120 mm; Body_With_Dia_2=129.73 mm; Bolt_support=320 mm; Bolt_support_2=160 mm; Bolt_support_Dia=16 mm  [stored 0.0524934 ft]; Bolt_support_lenght=95.1 mm; Bolt_support_lenght_2=105.1 mm; Bottom_profile=37.55 mm; D1=105.5 mm; DN=150.2 mm; FOD=142.5 mm; Fillet_Length=8 mm  [stored 0.0262467 ft]; Flange_thickness=19 mm; H3=590 mm; ID=75.1 mm; L=480 mm; L1=497 mm; L_Ref=488.5 mm; PG_Dia=50.07 mm; PG_Ref=80 mm; PG_depth=11.2 mm  [stored 0.0367454 ft]; PG_ref=85.1 mm; Pilot_Dia_1=31 mm; Pilot_Dia_2=62 mm; Pilot_Dia_3=20.67 mm; Pilot_Dia_4=10.33 mm; Pilot_Dia_5=6.89 mm; Pilot_top_1=361.25 mm; Pilot_top_ref=86.25 mm; Profile1_Height=230 mm; Profile1_Length=38.51 mm; Profile1_Length_2=25.68 mm; Profile_Dia=8 mm  [stored 0.0262467 ft]; Profile_Dia_2=8 mm  [stored 0.0262467 ft]; Profile_Dia_3=16 mm  [stored 0.0524934 ft]; Top_Profile=192 mm; Top_Profile_Ref=197 mm; Top_Ref=275 mm; Top_Ref_2=318.13 mm; W=410 mm; W_Ref=406 mm
- 879-0150-10-144002199A0_DN150_PN10/16: Body_Collar_Dia=50 mm; Body_Collar_Dia_2=43.05 mm; Body_Flange_Dia=154.84 mm; Body_Flange_Dia_2=171.43 mm; Body_Height_1=120 mm; Body_Height_2=60 mm; Body_Height_3=68 mm; Body_Height_4=75 mm; Body_Top_Dia=21.52 mm; Body_Top_Dia_2=17.94 mm; Body_With_Dia=120 mm; Body_With_Dia_2=129.73 mm; Bolt_support=320 mm; Bolt_support_2=160 mm; Bolt_support_Dia=16 mm  [stored 0.0524934 ft]; Bolt_support_lenght=95.15 mm; Bolt_support_lenght_2=105.15 mm; Bottom_profile=37.58 mm; D1=105.5 mm; DN=150.3 mm; FOD=142.5 mm; Fillet_Length=8 mm  [stored 0.0262467 ft]; Flange_thickness=19 mm; H3=607 mm; ID=75.15 mm; L=480 mm; L1=497 mm; L_Ref=488.5 mm; PG_Dia=50.1 mm; PG_Ref=80 mm; PG_depth=11.2 mm  [stored 0.0367454 ft]; PG_ref=85.15 mm; Pilot_Dia_1=31 mm; Pilot_Dia_2=62 mm; Pilot_Dia_3=20.67 mm; Pilot_Dia_4=10.33 mm; Pilot_Dia_5=6.89 mm; Pilot_top_1=373.75 mm; Pilot_top_ref=90.75 mm; Profile1_Height=230 mm; Profile1_Length=38.51 mm; Profile1_Length_2=25.68 mm; Profile_Dia=8 mm  [stored 0.0262467 ft]; Profile_Dia_2=8 mm  [stored 0.0262467 ft]; Profile_Dia_3=16 mm  [stored 0.0524934 ft]; Top_Profile=192 mm; Top_Profile_Ref=197 mm; Top_Ref=283 mm; Top_Ref_2=328.38 mm; W=410 mm; W_Ref=406 mm
- 879-0150-10-14400229999_DN150_PN10/16: Body_Collar_Dia=50 mm; Body_Collar_Dia_2=43.05 mm; Body_Flange_Dia=154.84 mm; Body_Flange_Dia_2=171.43 mm; Body_Height_1=120 mm; Body_Height_2=60 mm; Body_Height_3=60 mm; Body_Height_4=75 mm; Body_Top_Dia=21.52 mm; Body_Top_Dia_2=17.94 mm; Body_With_Dia=120 mm; Body_With_Dia_2=129.73 mm; Bolt_support=320 mm; Bolt_support_2=160 mm; Bolt_support_Dia=16 mm  [stored 0.0524934 ft]; Bolt_support_lenght=95.2 mm; Bolt_support_lenght_2=105.2 mm; Bottom_profile=37.6 mm; D1=105.5 mm; DN=150.4 mm; FOD=142.5 mm; Fillet_Length=8 mm  [stored 0.0262467 ft]; Flange_thickness=19 mm; H3=590 mm; ID=75.2 mm; L=480 mm; L1=497 mm; L_Ref=488.5 mm; PG_Dia=50.13 mm; PG_Ref=80 mm; PG_depth=11.2 mm  [stored 0.0367454 ft]; PG_ref=85.2 mm; Pilot_Dia_1=31 mm; Pilot_Dia_2=62 mm; Pilot_Dia_3=20.67 mm; Pilot_Dia_4=10.33 mm; Pilot_Dia_5=6.89 mm; Pilot_top_1=361.25 mm; Pilot_top_ref=86.25 mm; Profile1_Height=230 mm; Profile1_Length=38.51 mm; Profile1_Length_2=25.68 mm; Profile_Dia=8 mm  [stored 0.0262467 ft]; Profile_Dia_2=8 mm  [stored 0.0262467 ft]; Profile_Dia_3=16 mm  [stored 0.0524934 ft]; Top_Profile=192 mm; Top_Profile_Ref=197 mm; Top_Ref=275 mm; Top_Ref_2=318.13 mm; W=410 mm; W_Ref=406 mm
- 879-0150-10-144002299A0_DN150_PN10/16: Body_Collar_Dia=50 mm; Body_Collar_Dia_2=43.05 mm; Body_Flange_Dia=154.84 mm; Body_Flange_Dia_2=171.43 mm; Body_Height_1=120 mm; Body_Height_2=60 mm; Body_Height_3=68 mm; Body_Height_4=75 mm; Body_Top_Dia=21.52 mm; Body_Top_Dia_2=17.94 mm; Body_With_Dia=120 mm; Body_With_Dia_2=129.73 mm; Bolt_support=320 mm; Bolt_support_2=160 mm; Bolt_support_Dia=16 mm  [stored 0.0524934 ft]; Bolt_support_lenght=95.25 mm; Bolt_support_lenght_2=105.25 mm; Bottom_profile=37.63 mm; D1=105.5 mm; DN=150.5 mm; FOD=142.5 mm; Fillet_Length=8 mm  [stored 0.0262467 ft]; Flange_thickness=19 mm; H3=607 mm; ID=75.25 mm; L=480 mm; L1=497 mm; L_Ref=488.5 mm; PG_Dia=50.17 mm; PG_Ref=80 mm; PG_depth=11.2 mm  [stored 0.0367454 ft]; PG_ref=85.25 mm; Pilot_Dia_1=31 mm; Pilot_Dia_2=62 mm; Pilot_Dia_3=20.67 mm; Pilot_Dia_4=10.33 mm; Pilot_Dia_5=6.89 mm; Pilot_top_1=373.75 mm; Pilot_top_ref=90.75 mm; Profile1_Height=230 mm; Profile1_Length=38.51 mm; Profile1_Length_2=25.68 mm; Profile_Dia=8 mm  [stored 0.0262467 ft]; Profile_Dia_2=8 mm  [stored 0.0262467 ft]; Profile_Dia_3=16 mm  [stored 0.0524934 ft]; Top_Profile=192 mm; Top_Profile_Ref=197 mm; Top_Ref=283 mm; Top_Ref_2=328.38 mm; W=410 mm; W_Ref=406 mm
- 879-0150-10-14400239999_DN150_PN10/16: Body_Collar_Dia=50 mm; Body_Collar_Dia_2=43.05 mm; Body_Flange_Dia=154.84 mm; Body_Flange_Dia_2=171.43 mm; Body_Height_1=120 mm; Body_Height_2=60 mm; Body_Height_3=60 mm; Body_Height_4=75 mm; Body_Top_Dia=21.52 mm; Body_Top_Dia_2=17.94 mm; Body_With_Dia=120 mm; Body_With_Dia_2=129.73 mm; Bolt_support=320 mm; Bolt_support_2=160 mm; Bolt_support_Dia=16 mm  [stored 0.0524934 ft]; Bolt_support_lenght=95.3 mm; Bolt_support_lenght_2=105.3 mm; Bottom_profile=37.65 mm; D1=105.5 mm; DN=150.6 mm; FOD=142.5 mm; Fillet_Length=8 mm  [stored 0.0262467 ft]; Flange_thickness=19 mm; H3=590 mm; ID=75.3 mm; L=480 mm; L1=497 mm; L_Ref=488.5 mm; PG_Dia=50.2 mm; PG_Ref=80 mm; PG_depth=11.2 mm  [stored 0.0367454 ft]; PG_ref=85.3 mm; Pilot_Dia_1=31 mm; Pilot_Dia_2=62 mm; Pilot_Dia_3=20.67 mm; Pilot_Dia_4=10.33 mm; Pilot_Dia_5=6.89 mm; Pilot_top_1=361.25 mm; Pilot_top_ref=86.25 mm; Profile1_Height=230 mm; Profile1_Length=38.51 mm; Profile1_Length_2=25.68 mm; Profile_Dia=8 mm  [stored 0.0262467 ft]; Profile_Dia_2=8 mm  [stored 0.0262467 ft]; Profile_Dia_3=16 mm  [stored 0.0524934 ft]; Top_Profile=192 mm; Top_Profile_Ref=197 mm; Top_Ref=275 mm; Top_Ref_2=318.13 mm; W=410 mm; W_Ref=406 mm
- 879-0150-10-144002399A0_DN150_PN10/16: Body_Collar_Dia=50 mm; Body_Collar_Dia_2=43.05 mm; Body_Flange_Dia=154.84 mm; Body_Flange_Dia_2=171.43 mm; Body_Height_1=120 mm; Body_Height_2=60 mm; Body_Height_3=68 mm; Body_Height_4=75 mm; Body_Top_Dia=21.52 mm; Body_Top_Dia_2=17.94 mm; Body_With_Dia=120 mm; Body_With_Dia_2=129.73 mm; Bolt_support=320 mm; Bolt_support_2=160 mm; Bolt_support_Dia=16 mm  [stored 0.0524934 ft]; Bolt_support_lenght=95.35 mm; Bolt_support_lenght_2=105.35 mm; Bottom_profile=37.68 mm; D1=105.5 mm; DN=150.7 mm; FOD=142.5 mm; Fillet_Length=8 mm  [stored 0.0262467 ft]; Flange_thickness=19 mm; H3=607 mm; ID=75.35 mm; L=480 mm; L1=497 mm; L_Ref=488.5 mm; PG_Dia=50.23 mm; PG_Ref=80 mm; PG_depth=11.2 mm  [stored 0.0367454 ft]; PG_ref=85.35 mm; Pilot_Dia_1=31 mm; Pilot_Dia_2=62 mm; Pilot_Dia_3=20.67 mm; Pilot_Dia_4=10.33 mm; Pilot_Dia_5=6.89 mm; Pilot_top_1=373.75 mm; Pilot_top_ref=90.75 mm; Profile1_Height=230 mm; Profile1_Length=38.51 mm; Profile1_Length_2=25.68 mm; Profile_Dia=8 mm  [stored 0.0262467 ft]; Profile_Dia_2=8 mm  [stored 0.0262467 ft]; Profile_Dia_3=16 mm  [stored 0.0524934 ft]; Top_Profile=192 mm; Top_Profile_Ref=197 mm; Top_Ref=283 mm; Top_Ref_2=328.38 mm; W=410 mm; W_Ref=406 mm
- 879-0200-10-04400209999_DN200_PN10: Body_Collar_Dia=62.5 mm; Body_Collar_Dia_2=53.81 mm; Body_Flange_Dia=193.55 mm; Body_Flange_Dia_2=214.29 mm; Body_Height_1=150 mm; Body_Height_2=75 mm; Body_Height_3=75 mm; Body_Height_4=90 mm; Body_Top_Dia=26.91 mm; Body_Top_Dia_2=22.42 mm; Body_With_Dia=150 mm; Body_With_Dia_2=162.16 mm; Bolt_support=400 mm; Bolt_support_2=200 mm; Bolt_support_Dia=20 mm; Bolt_support_lenght=120 mm; Bolt_support_lenght_2=130 mm; Bottom_profile=50 mm; D1=133 mm; DN=200 mm; FOD=170 mm; Fillet_Length=10 mm  [stored 0.0328084 ft]; Flange_thickness=20 mm; H3=670 mm; ID=100 mm; L=600 mm; L1=617 mm; L_Ref=608.5 mm; PG_Dia=66.67 mm; PG_Ref=100 mm; PG_depth=14 mm  [stored 0.0459318 ft]; PG_ref=110 mm; Pilot_Dia_1=38.5 mm; Pilot_Dia_2=77 mm; Pilot_Dia_3=25.67 mm; Pilot_Dia_4=12.83 mm; Pilot_Dia_5=8.56 mm; Pilot_top_1=417.5 mm; Pilot_top_ref=82.5 mm; Profile1_Height=273 mm; Profile1_Length=45.95 mm; Profile1_Length_2=30.63 mm; Profile_Dia=10 mm  [stored 0.0328084 ft]; Profile_Dia_2=10 mm  [stored 0.0328084 ft]; Profile_Dia_3=20 mm; Top_Profile=240 mm; Top_Profile_Ref=245 mm; Top_Ref=335 mm; Top_Ref_2=376.25 mm; W=510 mm; W_Ref=505 mm
- 879-0200-10-044002099A0_DN200_PN10: Body_Collar_Dia=62.5 mm; Body_Collar_Dia_2=53.81 mm; Body_Flange_Dia=193.55 mm; Body_Flange_Dia_2=214.29 mm; Body_Height_1=150 mm; Body_Height_2=75 mm; Body_Height_3=100 mm; Body_Height_4=90 mm; Body_Top_Dia=26.91 mm; Body_Top_Dia_2=22.42 mm; Body_With_Dia=150 mm; Body_With_Dia_2=162.16 mm; Bolt_support=400 mm; Bolt_support_2=200 mm; Bolt_support_Dia=20 mm; Bolt_support_lenght=120.05 mm; Bolt_support_lenght_2=130.05 mm; Bottom_profile=50.03 mm; D1=133 mm; DN=200.1 mm; FOD=170 mm; Fillet_Length=10 mm  [stored 0.0328084 ft]; Flange_thickness=20 mm; H3=774 mm; ID=100.05 mm; L=600 mm; L1=617 mm; L_Ref=608.5 mm; PG_Dia=66.7 mm; PG_Ref=100 mm; PG_depth=14 mm  [stored 0.0459318 ft]; PG_ref=110.05 mm; Pilot_Dia_1=38.5 mm; Pilot_Dia_2=77 mm; Pilot_Dia_3=25.67 mm; Pilot_Dia_4=12.83 mm; Pilot_Dia_5=8.56 mm; Pilot_top_1=482 mm; Pilot_top_ref=122 mm; Profile1_Height=275 mm; Profile1_Length=45.95 mm; Profile1_Length_2=30.63 mm; Profile_Dia=10 mm  [stored 0.0328084 ft]; Profile_Dia_2=10 mm  [stored 0.0328084 ft]; Profile_Dia_3=20 mm; Top_Profile=240 mm; Top_Profile_Ref=245 mm; Top_Ref=360 mm; Top_Ref_2=421 mm; W=510 mm; W_Ref=505 mm
- 879-0200-10-04400219999_DN200_PN10: Body_Collar_Dia=62.5 mm; Body_Collar_Dia_2=53.81 mm; Body_Flange_Dia=193.55 mm; Body_Flange_Dia_2=214.29 mm; Body_Height_1=150 mm; Body_Height_2=75 mm; Body_Height_3=75 mm; Body_Height_4=90 mm; Body_Top_Dia=26.91 mm; Body_Top_Dia_2=22.42 mm; Body_With_Dia=150 mm; Body_With_Dia_2=162.16 mm; Bolt_support=400 mm; Bolt_support_2=200 mm; Bolt_support_Dia=20 mm; Bolt_support_lenght=120.1 mm; Bolt_support_lenght_2=130.1 mm; Bottom_profile=50.05 mm; D1=133 mm; DN=200.2 mm; FOD=170 mm; Fillet_Length=10 mm  [stored 0.0328084 ft]; Flange_thickness=20 mm; H3=670 mm; ID=100.1 mm; L=600 mm; L1=617 mm; L_Ref=608.5 mm; PG_Dia=66.73 mm; PG_Ref=100 mm; PG_depth=14 mm  [stored 0.0459318 ft]; PG_ref=110.1 mm; Pilot_Dia_1=38.5 mm; Pilot_Dia_2=77 mm; Pilot_Dia_3=25.67 mm; Pilot_Dia_4=12.83 mm; Pilot_Dia_5=8.56 mm; Pilot_top_1=417.5 mm; Pilot_top_ref=82.5 mm; Profile1_Height=273 mm; Profile1_Length=45.95 mm; Profile1_Length_2=30.63 mm; Profile_Dia=10 mm  [stored 0.0328084 ft]; Profile_Dia_2=10 mm  [stored 0.0328084 ft]; Profile_Dia_3=20 mm; Top_Profile=240 mm; Top_Profile_Ref=245 mm; Top_Ref=335 mm; Top_Ref_2=376.25 mm; W=510 mm; W_Ref=505 mm
- 879-0200-10-044002199A0_DN200_PN10: Body_Collar_Dia=62.5 mm; Body_Collar_Dia_2=53.81 mm; Body_Flange_Dia=193.55 mm; Body_Flange_Dia_2=214.29 mm; Body_Height_1=150 mm; Body_Height_2=75 mm; Body_Height_3=86 mm; Body_Height_4=90 mm; Body_Top_Dia=26.91 mm; Body_Top_Dia_2=22.42 mm; Body_With_Dia=150 mm; Body_With_Dia_2=162.16 mm; Bolt_support=400 mm; Bolt_support_2=200 mm; Bolt_support_Dia=20 mm; Bolt_support_lenght=120.15 mm; Bolt_support_lenght_2=130.15 mm; Bottom_profile=50.08 mm; D1=133 mm; DN=200.3 mm; FOD=170 mm; Fillet_Length=10 mm  [stored 0.0328084 ft]; Flange_thickness=20 mm; H3=774 mm; ID=100.15 mm; L=600 mm; L1=617 mm; L_Ref=608.5 mm; PG_Dia=66.77 mm; PG_Ref=100 mm; PG_depth=14 mm  [stored 0.0459318 ft]; PG_ref=110.15 mm; Pilot_Dia_1=38.5 mm; Pilot_Dia_2=77 mm; Pilot_Dia_3=25.67 mm; Pilot_Dia_4=12.83 mm; Pilot_Dia_5=8.56 mm; Pilot_top_1=475 mm; Pilot_top_ref=129 mm; Profile1_Height=275 mm; Profile1_Length=45.95 mm; Profile1_Length_2=30.63 mm; Profile_Dia=10 mm  [stored 0.0328084 ft]; Profile_Dia_2=10 mm  [stored 0.0328084 ft]; Profile_Dia_3=20 mm; Top_Profile=240 mm; Top_Profile_Ref=245 mm; Top_Ref=346 mm; Top_Ref_2=410.5 mm; W=510 mm; W_Ref=505 mm
- 879-0200-10-04400229999_DN200_PN10: Body_Collar_Dia=62.5 mm; Body_Collar_Dia_2=53.81 mm; Body_Flange_Dia=193.55 mm; Body_Flange_Dia_2=214.29 mm; Body_Height_1=150 mm; Body_Height_2=75 mm; Body_Height_3=75 mm; Body_Height_4=90 mm; Body_Top_Dia=26.91 mm; Body_Top_Dia_2=22.42 mm; Body_With_Dia=150 mm; Body_With_Dia_2=162.16 mm; Bolt_support=400 mm; Bolt_support_2=200 mm; Bolt_support_Dia=20 mm; Bolt_support_lenght=120.2 mm; Bolt_support_lenght_2=130.2 mm; Bottom_profile=50.1 mm; D1=133 mm; DN=200.4 mm; FOD=170 mm; Fillet_Length=10 mm  [stored 0.0328084 ft]; Flange_thickness=20 mm; H3=670 mm; ID=100.2 mm; L=600 mm; L1=617 mm; L_Ref=608.5 mm; PG_Dia=66.8 mm; PG_Ref=100 mm; PG_depth=14 mm  [stored 0.0459318 ft]; PG_ref=110.2 mm; Pilot_Dia_1=38.5 mm; Pilot_Dia_2=77 mm; Pilot_Dia_3=25.67 mm; Pilot_Dia_4=12.83 mm; Pilot_Dia_5=8.56 mm; Pilot_top_1=417.5 mm; Pilot_top_ref=82.5 mm; Profile1_Height=273 mm; Profile1_Length=45.95 mm; Profile1_Length_2=30.63 mm; Profile_Dia=10 mm  [stored 0.0328084 ft]; Profile_Dia_2=10 mm  [stored 0.0328084 ft]; Profile_Dia_3=20 mm; Top_Profile=240 mm; Top_Profile_Ref=245 mm; Top_Ref=335 mm; Top_Ref_2=376.25 mm; W=510 mm; W_Ref=505 mm
- 879-0200-10-044002299A0_DN200_PN10: Body_Collar_Dia=62.5 mm; Body_Collar_Dia_2=53.81 mm; Body_Flange_Dia=193.55 mm; Body_Flange_Dia_2=214.29 mm; Body_Height_1=150 mm; Body_Height_2=75 mm; Body_Height_3=100 mm; Body_Height_4=90 mm; Body_Top_Dia=26.91 mm; Body_Top_Dia_2=22.42 mm; Body_With_Dia=150 mm; Body_With_Dia_2=162.16 mm; Bolt_support=400 mm; Bolt_support_2=200 mm; Bolt_support_Dia=20 mm; Bolt_support_lenght=120.25 mm; Bolt_support_lenght_2=130.25 mm; Bottom_profile=50.13 mm; D1=133 mm; DN=200.5 mm; FOD=170 mm; Fillet_Length=10 mm  [stored 0.0328084 ft]; Flange_thickness=20 mm; H3=774 mm; ID=100.25 mm; L=600 mm; L1=617 mm; L_Ref=608.5 mm; PG_Dia=66.83 mm; PG_Ref=100 mm; PG_depth=14 mm  [stored 0.0459318 ft]; PG_ref=110.25 mm; Pilot_Dia_1=38.5 mm; Pilot_Dia_2=77 mm; Pilot_Dia_3=25.67 mm; Pilot_Dia_4=12.83 mm; Pilot_Dia_5=8.56 mm; Pilot_top_1=482 mm; Pilot_top_ref=122 mm; Profile1_Height=275 mm; Profile1_Length=45.95 mm; Profile1_Length_2=30.63 mm; Profile_Dia=10 mm  [stored 0.0328084 ft]; Profile_Dia_2=10 mm  [stored 0.0328084 ft]; Profile_Dia_3=20 mm; Top_Profile=240 mm; Top_Profile_Ref=245 mm; Top_Ref=360 mm; Top_Ref_2=421 mm; W=510 mm; W_Ref=505 mm
- 879-0200-10-04400239999_DN200_PN10: Body_Collar_Dia=62.5 mm; Body_Collar_Dia_2=53.81 mm; Body_Flange_Dia=193.55 mm; Body_Flange_Dia_2=214.29 mm; Body_Height_1=150 mm; Body_Height_2=75 mm; Body_Height_3=75 mm; Body_Height_4=90 mm; Body_Top_Dia=26.91 mm; Body_Top_Dia_2=22.42 mm; Body_With_Dia=150 mm; Body_With_Dia_2=162.16 mm; Bolt_support=400 mm; Bolt_support_2=200 mm; Bolt_support_Dia=20 mm; Bolt_support_lenght=120.3 mm; Bolt_support_lenght_2=130.3 mm; Bottom_profile=50.15 mm; D1=133 mm; DN=200.6 mm; FOD=170 mm; Fillet_Length=10 mm  [stored 0.0328084 ft]; Flange_thickness=20 mm; H3=670 mm; ID=100.3 mm; L=600 mm; L1=617 mm; L_Ref=608.5 mm; PG_Dia=66.87 mm; PG_Ref=100 mm; PG_depth=14 mm  [stored 0.0459318 ft]; PG_ref=110.3 mm; Pilot_Dia_1=38.5 mm; Pilot_Dia_2=77 mm; Pilot_Dia_3=25.67 mm; Pilot_Dia_4=12.83 mm; Pilot_Dia_5=8.56 mm; Pilot_top_1=417.5 mm; Pilot_top_ref=82.5 mm; Profile1_Height=273 mm; Profile1_Length=45.95 mm; Profile1_Length_2=30.63 mm; Profile_Dia=10 mm  [stored 0.0328084 ft]; Profile_Dia_2=10 mm  [stored 0.0328084 ft]; Profile_Dia_3=20 mm; Top_Profile=240 mm; Top_Profile_Ref=245 mm; Top_Ref=335 mm; Top_Ref_2=376.25 mm; W=510 mm; W_Ref=505 mm
- 879-0200-10-044002399A0_DN200_PN10: Body_Collar_Dia=62.5 mm; Body_Collar_Dia_2=53.81 mm; Body_Flange_Dia=193.55 mm; Body_Flange_Dia_2=214.29 mm; Body_Height_1=150 mm; Body_Height_2=75 mm; Body_Height_3=86 mm; Body_Height_4=90 mm; Body_Top_Dia=26.91 mm; Body_Top_Dia_2=22.42 mm; Body_With_Dia=150 mm; Body_With_Dia_2=162.16 mm; Bolt_support=400 mm; Bolt_support_2=200 mm; Bolt_support_Dia=20 mm; Bolt_support_lenght=120.35 mm; Bolt_support_lenght_2=130.35 mm; Bottom_profile=50.18 mm; D1=133 mm; DN=200.7 mm; FOD=170 mm; Fillet_Length=10 mm  [stored 0.0328084 ft]; Flange_thickness=20 mm; H3=774 mm; ID=100.35 mm; L=600 mm; L1=617 mm; L_Ref=608.5 mm; PG_Dia=66.9 mm; PG_Ref=100 mm; PG_depth=14 mm  [stored 0.0459318 ft]; PG_ref=110.35 mm; Pilot_Dia_1=38.5 mm; Pilot_Dia_2=77 mm; Pilot_Dia_3=25.67 mm; Pilot_Dia_4=12.83 mm; Pilot_Dia_5=8.56 mm; Pilot_top_1=475 mm; Pilot_top_ref=129 mm; Profile1_Height=275 mm; Profile1_Length=45.95 mm; Profile1_Length_2=30.63 mm; Profile_Dia=10 mm  [stored 0.0328084 ft]; Profile_Dia_2=10 mm  [stored 0.0328084 ft]; Profile_Dia_3=20 mm; Top_Profile=240 mm; Top_Profile_Ref=245 mm; Top_Ref=346 mm; Top_Ref_2=410.5 mm; W=510 mm; W_Ref=505 mm
- 879-0200-10-14400209999_DN200_PN16: Body_Collar_Dia=62.5 mm; Body_Collar_Dia_2=53.81 mm; Body_Flange_Dia=193.55 mm; Body_Flange_Dia_2=214.29 mm; Body_Height_1=150 mm; Body_Height_2=75 mm; Body_Height_3=75 mm; Body_Height_4=90 mm; Body_Top_Dia=26.91 mm; Body_Top_Dia_2=22.42 mm; Body_With_Dia=150 mm; Body_With_Dia_2=162.16 mm; Bolt_support=400 mm; Bolt_support_2=200 mm; Bolt_support_Dia=20 mm; Bolt_support_lenght=120.4 mm; Bolt_support_lenght_2=130.4 mm; Bottom_profile=50.2 mm; D1=133 mm; DN=200.8 mm; FOD=170 mm; Fillet_Length=10 mm  [stored 0.0328084 ft]; Flange_thickness=20 mm; H3=670 mm; ID=100.4 mm; L=600 mm; L1=617 mm; L_Ref=608.5 mm; PG_Dia=66.93 mm; PG_Ref=100 mm; PG_depth=14 mm  [stored 0.0459318 ft]; PG_ref=110.4 mm; Pilot_Dia_1=38.5 mm; Pilot_Dia_2=77 mm; Pilot_Dia_3=25.67 mm; Pilot_Dia_4=12.83 mm; Pilot_Dia_5=8.56 mm; Pilot_top_1=417.5 mm; Pilot_top_ref=82.5 mm; Profile1_Height=273 mm; Profile1_Length=45.95 mm; Profile1_Length_2=30.63 mm; Profile_Dia=10 mm  [stored 0.0328084 ft]; Profile_Dia_2=10 mm  [stored 0.0328084 ft]; Profile_Dia_3=20 mm; Top_Profile=240 mm; Top_Profile_Ref=245 mm; Top_Ref=335 mm; Top_Ref_2=376.25 mm; W=510 mm; W_Ref=505 mm
- 879-0200-10-144002099A0_DN200_PN16: Body_Collar_Dia=62.5 mm; Body_Collar_Dia_2=53.81 mm; Body_Flange_Dia=193.55 mm; Body_Flange_Dia_2=214.29 mm; Body_Height_1=150 mm; Body_Height_2=75 mm; Body_Height_3=100 mm; Body_Height_4=90 mm; Body_Top_Dia=26.91 mm; Body_Top_Dia_2=22.42 mm; Body_With_Dia=150 mm; Body_With_Dia_2=162.16 mm; Bolt_support=400 mm; Bolt_support_2=200 mm; Bolt_support_Dia=20 mm; Bolt_support_lenght=120.45 mm; Bolt_support_lenght_2=130.45 mm; Bottom_profile=50.23 mm; D1=133 mm; DN=200.9 mm; FOD=170 mm; Fillet_Length=10 mm  [stored 0.0328084 ft]; Flange_thickness=20 mm; H3=774 mm; ID=100.45 mm; L=600 mm; L1=617 mm; L_Ref=608.5 mm; PG_Dia=66.97 mm; PG_Ref=100 mm; PG_depth=14 mm  [stored 0.0459318 ft]; PG_ref=110.45 mm; Pilot_Dia_1=38.5 mm; Pilot_Dia_2=77 mm; Pilot_Dia_3=25.67 mm; Pilot_Dia_4=12.83 mm; Pilot_Dia_5=8.56 mm; Pilot_top_1=482 mm; Pilot_top_ref=122 mm; Profile1_Height=275 mm; Profile1_Length=45.95 mm; Profile1_Length_2=30.63 mm; Profile_Dia=10 mm  [stored 0.0328084 ft]; Profile_Dia_2=10 mm  [stored 0.0328084 ft]; Profile_Dia_3=20 mm; Top_Profile=240 mm; Top_Profile_Ref=245 mm; Top_Ref=360 mm; Top_Ref_2=421 mm; W=510 mm; W_Ref=505 mm
- 879-0200-10-14400219999_DN200_PN16: Body_Collar_Dia=62.5 mm; Body_Collar_Dia_2=53.81 mm; Body_Flange_Dia=193.55 mm; Body_Flange_Dia_2=214.29 mm; Body_Height_1=150 mm; Body_Height_2=75 mm; Body_Height_3=75 mm; Body_Height_4=90 mm; Body_Top_Dia=26.91 mm; Body_Top_Dia_2=22.42 mm; Body_With_Dia=150 mm; Body_With_Dia_2=162.16 mm; Bolt_support=400 mm; Bolt_support_2=200 mm; Bolt_support_Dia=20 mm; Bolt_support_lenght=120.06 mm; Bolt_support_lenght_2=130.06 mm; Bottom_profile=50.03 mm; D1=133 mm; DN=200.11 mm; FOD=170 mm; Fillet_Length=10 mm  [stored 0.0328084 ft]; Flange_thickness=20 mm; H3=670 mm; ID=100.06 mm; L=600 mm; L1=617 mm; L_Ref=608.5 mm; PG_Dia=66.7 mm; PG_Ref=100 mm; PG_depth=14 mm  [stored 0.0459318 ft]; PG_ref=110.06 mm; Pilot_Dia_1=38.5 mm; Pilot_Dia_2=77 mm; Pilot_Dia_3=25.67 mm; Pilot_Dia_4=12.83 mm; Pilot_Dia_5=8.56 mm; Pilot_top_1=417.5 mm; Pilot_top_ref=82.5 mm; Profile1_Height=273 mm; Profile1_Length=45.95 mm; Profile1_Length_2=30.63 mm; Profile_Dia=10 mm  [stored 0.0328084 ft]; Profile_Dia_2=10 mm  [stored 0.0328084 ft]; Profile_Dia_3=20 mm; Top_Profile=240 mm; Top_Profile_Ref=245 mm; Top_Ref=335 mm; Top_Ref_2=376.25 mm; W=510 mm; W_Ref=505 mm
- 879-0200-10-144002199A0_DN200_PN16: Body_Collar_Dia=62.5 mm; Body_Collar_Dia_2=53.81 mm; Body_Flange_Dia=193.55 mm; Body_Flange_Dia_2=214.29 mm; Body_Height_1=150 mm; Body_Height_2=75 mm; Body_Height_3=86 mm; Body_Height_4=90 mm; Body_Top_Dia=26.91 mm; Body_Top_Dia_2=22.42 mm; Body_With_Dia=150 mm; Body_With_Dia_2=162.16 mm; Bolt_support=400 mm; Bolt_support_2=200 mm; Bolt_support_Dia=20 mm; Bolt_support_lenght=120.06 mm; Bolt_support_lenght_2=130.06 mm; Bottom_profile=50.03 mm; D1=133 mm; DN=200.12 mm; FOD=170 mm; Fillet_Length=10 mm  [stored 0.0328084 ft]; Flange_thickness=20 mm; H3=774 mm; ID=100.06 mm; L=600 mm; L1=617 mm; L_Ref=608.5 mm; PG_Dia=66.71 mm; PG_Ref=100 mm; PG_depth=14 mm  [stored 0.0459318 ft]; PG_ref=110.06 mm; Pilot_Dia_1=38.5 mm; Pilot_Dia_2=77 mm; Pilot_Dia_3=25.67 mm; Pilot_Dia_4=12.83 mm; Pilot_Dia_5=8.56 mm; Pilot_top_1=475 mm; Pilot_top_ref=129 mm; Profile1_Height=275 mm; Profile1_Length=45.95 mm; Profile1_Length_2=30.63 mm; Profile_Dia=10 mm  [stored 0.0328084 ft]; Profile_Dia_2=10 mm  [stored 0.0328084 ft]; Profile_Dia_3=20 mm; Top_Profile=240 mm; Top_Profile_Ref=245 mm; Top_Ref=346 mm; Top_Ref_2=410.5 mm; W=510 mm; W_Ref=505 mm
- 879-0200-10-14400229999_DN200_PN16: Body_Collar_Dia=62.5 mm; Body_Collar_Dia_2=53.81 mm; Body_Flange_Dia=193.55 mm; Body_Flange_Dia_2=214.29 mm; Body_Height_1=150 mm; Body_Height_2=75 mm; Body_Height_3=75 mm; Body_Height_4=90 mm; Body_Top_Dia=26.91 mm; Body_Top_Dia_2=22.42 mm; Body_With_Dia=150 mm; Body_With_Dia_2=162.16 mm; Bolt_support=400 mm; Bolt_support_2=200 mm; Bolt_support_Dia=20 mm; Bolt_support_lenght=120.07 mm; Bolt_support_lenght_2=130.07 mm; Bottom_profile=50.03 mm; D1=133 mm; DN=200.13 mm; FOD=170 mm; Fillet_Length=10 mm  [stored 0.0328084 ft]; Flange_thickness=20 mm; H3=670 mm; ID=100.07 mm; L=600 mm; L1=617 mm; L_Ref=608.5 mm; PG_Dia=66.71 mm; PG_Ref=100 mm; PG_depth=14 mm  [stored 0.0459318 ft]; PG_ref=110.07 mm; Pilot_Dia_1=38.5 mm; Pilot_Dia_2=77 mm; Pilot_Dia_3=25.67 mm; Pilot_Dia_4=12.83 mm; Pilot_Dia_5=8.56 mm; Pilot_top_1=417.5 mm; Pilot_top_ref=82.5 mm; Profile1_Height=273 mm; Profile1_Length=45.95 mm; Profile1_Length_2=30.63 mm; Profile_Dia=10 mm  [stored 0.0328084 ft]; Profile_Dia_2=10 mm  [stored 0.0328084 ft]; Profile_Dia_3=20 mm; Top_Profile=240 mm; Top_Profile_Ref=245 mm; Top_Ref=335 mm; Top_Ref_2=376.25 mm; W=510 mm; W_Ref=505 mm
- 879-0200-10-144002299A0_DN200_PN16: Body_Collar_Dia=62.5 mm; Body_Collar_Dia_2=53.81 mm; Body_Flange_Dia=193.55 mm; Body_Flange_Dia_2=214.29 mm; Body_Height_1=150 mm; Body_Height_2=75 mm; Body_Height_3=100 mm; Body_Height_4=90 mm; Body_Top_Dia=26.91 mm; Body_Top_Dia_2=22.42 mm; Body_With_Dia=150 mm; Body_With_Dia_2=162.16 mm; Bolt_support=400 mm; Bolt_support_2=200 mm; Bolt_support_Dia=20 mm; Bolt_support_lenght=120.07 mm; Bolt_support_lenght_2=130.07 mm; Bottom_profile=50.04 mm; D1=133 mm; DN=200.14 mm; FOD=170 mm; Fillet_Length=10 mm  [stored 0.0328084 ft]; Flange_thickness=20 mm; H3=774 mm; ID=100.07 mm; L=600 mm; L1=617 mm; L_Ref=608.5 mm; PG_Dia=66.71 mm; PG_Ref=100 mm; PG_depth=14 mm  [stored 0.0459318 ft]; PG_ref=110.07 mm; Pilot_Dia_1=38.5 mm; Pilot_Dia_2=77 mm; Pilot_Dia_3=25.67 mm; Pilot_Dia_4=12.83 mm; Pilot_Dia_5=8.56 mm; Pilot_top_1=482 mm; Pilot_top_ref=122 mm; Profile1_Height=275 mm; Profile1_Length=45.95 mm; Profile1_Length_2=30.63 mm; Profile_Dia=10 mm  [stored 0.0328084 ft]; Profile_Dia_2=10 mm  [stored 0.0328084 ft]; Profile_Dia_3=20 mm; Top_Profile=240 mm; Top_Profile_Ref=245 mm; Top_Ref=360 mm; Top_Ref_2=421 mm; W=510 mm; W_Ref=505 mm
- 879-0200-10-14400239999_DN200_PN16: Body_Collar_Dia=62.5 mm; Body_Collar_Dia_2=53.81 mm; Body_Flange_Dia=193.55 mm; Body_Flange_Dia_2=214.29 mm; Body_Height_1=150 mm; Body_Height_2=75 mm; Body_Height_3=75 mm; Body_Height_4=90 mm; Body_Top_Dia=26.91 mm; Body_Top_Dia_2=22.42 mm; Body_With_Dia=150 mm; Body_With_Dia_2=162.16 mm; Bolt_support=400 mm; Bolt_support_2=200 mm; Bolt_support_Dia=20 mm; Bolt_support_lenght=120.08 mm; Bolt_support_lenght_2=130.08 mm; Bottom_profile=50.04 mm; D1=133 mm; DN=200.15 mm; FOD=170 mm; Fillet_Length=10 mm  [stored 0.0328084 ft]; Flange_thickness=20 mm; H3=670 mm; ID=100.08 mm; L=600 mm; L1=617 mm; L_Ref=608.5 mm; PG_Dia=66.72 mm; PG_Ref=100 mm; PG_depth=14 mm  [stored 0.0459318 ft]; PG_ref=110.08 mm; Pilot_Dia_1=38.5 mm; Pilot_Dia_2=77 mm; Pilot_Dia_3=25.67 mm; Pilot_Dia_4=12.83 mm; Pilot_Dia_5=8.56 mm; Pilot_top_1=417.5 mm; Pilot_top_ref=82.5 mm; Profile1_Height=273 mm; Profile1_Length=45.95 mm; Profile1_Length_2=30.63 mm; Profile_Dia=10 mm  [stored 0.0328084 ft]; Profile_Dia_2=10 mm  [stored 0.0328084 ft]; Profile_Dia_3=20 mm; Top_Profile=240 mm; Top_Profile_Ref=245 mm; Top_Ref=335 mm; Top_Ref_2=376.25 mm; W=510 mm; W_Ref=505 mm
- 879-0200-10-144002399A0_DN200_PN16: Body_Collar_Dia=62.5 mm; Body_Collar_Dia_2=53.81 mm; Body_Flange_Dia=193.55 mm; Body_Flange_Dia_2=214.29 mm; Body_Height_1=150 mm; Body_Height_2=75 mm; Body_Height_3=86 mm; Body_Height_4=90 mm; Body_Top_Dia=26.91 mm; Body_Top_Dia_2=22.42 mm; Body_With_Dia=150 mm; Body_With_Dia_2=162.16 mm; Bolt_support=400 mm; Bolt_support_2=200 mm; Bolt_support_Dia=20 mm; Bolt_support_lenght=120.08 mm; Bolt_support_lenght_2=130.08 mm; Bottom_profile=50.04 mm; D1=133 mm; DN=200.16 mm; FOD=170 mm; Fillet_Length=10 mm  [stored 0.0328084 ft]; Flange_thickness=20 mm; H3=774 mm; ID=100.08 mm; L=600 mm; L1=617 mm; L_Ref=608.5 mm; PG_Dia=66.72 mm; PG_Ref=100 mm; PG_depth=14 mm  [stored 0.0459318 ft]; PG_ref=110.08 mm; Pilot_Dia_1=38.5 mm; Pilot_Dia_2=77 mm; Pilot_Dia_3=25.67 mm; Pilot_Dia_4=12.83 mm; Pilot_Dia_5=8.56 mm; Pilot_top_1=475 mm; Pilot_top_ref=129 mm; Profile1_Height=275 mm; Profile1_Length=45.95 mm; Profile1_Length_2=30.63 mm; Profile_Dia=10 mm  [stored 0.0328084 ft]; Profile_Dia_2=10 mm  [stored 0.0328084 ft]; Profile_Dia_3=20 mm; Top_Profile=240 mm; Top_Profile_Ref=245 mm; Top_Ref=346 mm; Top_Ref_2=410.5 mm; W=510 mm; W_Ref=505 mm

note: [stored X ft] marks values corroborated as IEEE doubles in the binary element streams (Revit-internal decimal feet)

## geometry (parser evidence)
native form markers: Sweep x3
no freeform markers — native parametric forms only
